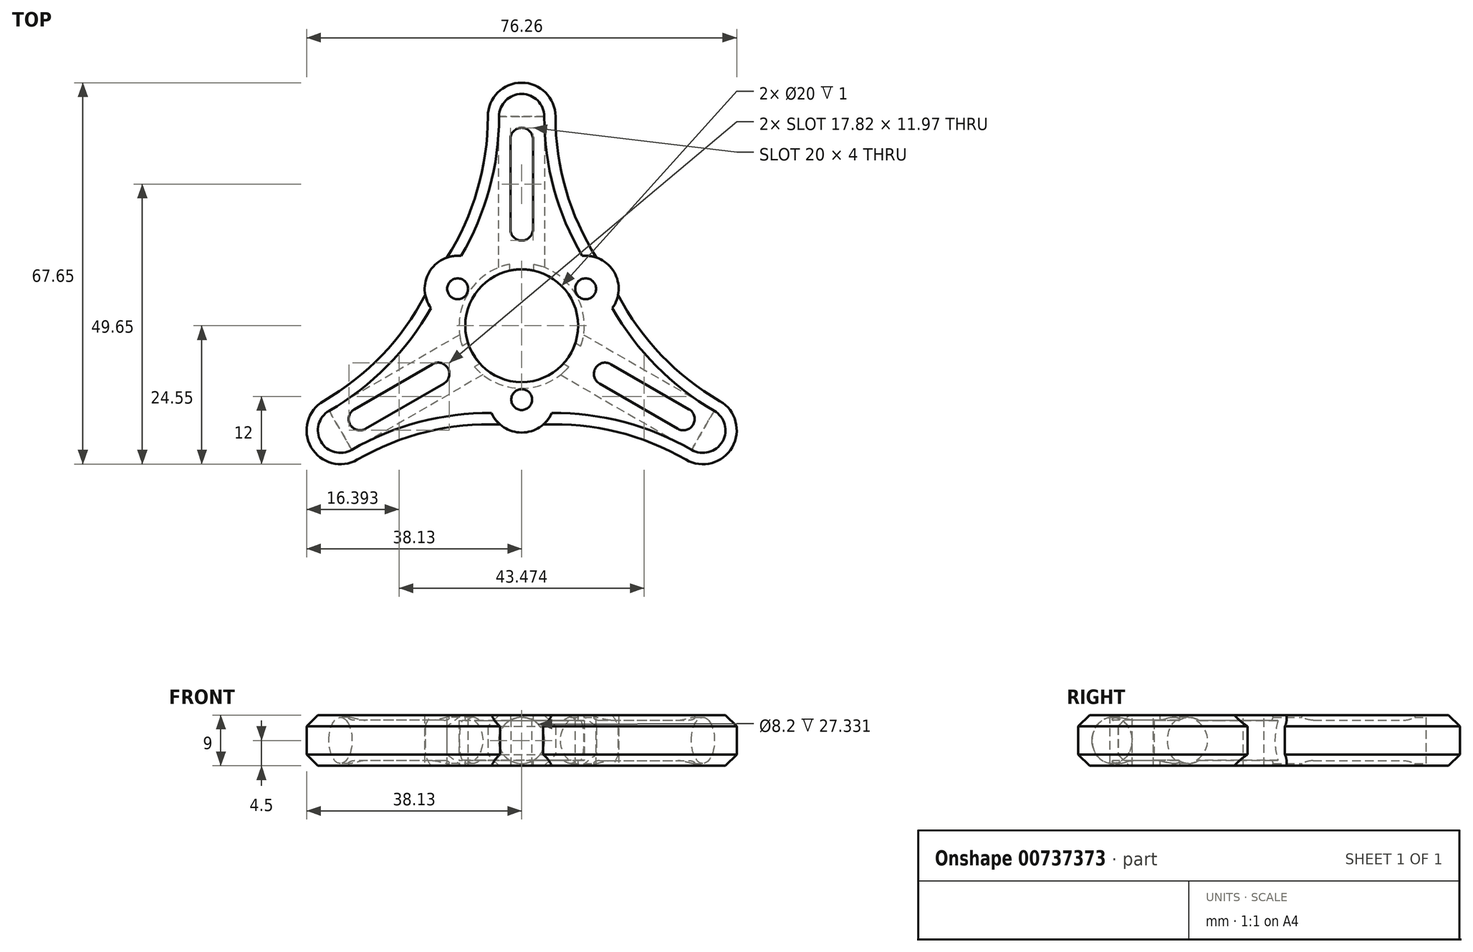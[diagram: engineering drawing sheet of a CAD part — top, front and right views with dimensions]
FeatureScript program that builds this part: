
annotation { "Feature Type Name" : "Feature", "Feature Type Description" : "" }
export const myFeature = defineFeature(function(context is Context, id is Id, definition is map)
    precondition{}
    {
        {
            var Q0;
            Q0=qCreatedBy(makeId("Top.planeOp"),FACE);
            var sketch = newSketch(context, id + "F0", { "sketchPlane" : qUnion([Q0])});
            skCircle(sketch, "E0", {"center": v(0, 0) * mm, "radius": 11.1 * mm});
            skCircle(sketch, "E1", {"center": v(0, 0) * mm, "radius": 13.1 * mm});
            skSolve(sketch);
        }
        {
            var Q0;
            Q0 = qSketchRegion(id + "F0", true);
            extrude(context, id + "F1", {"entities" : qUnion([Q0]), "depth" : 3.5 * mm, "offsetDistance" : 25 * mm});
        }
        {
            var Q0;
            Q0=makeQuery(id+"F1.opExtrude","CAP_FACE",FACE,{"disambiguationData":[OSD([sQuery(id+"F0.wireOp",EDGE,"E0"),sQuery(id+"F0.wireOp",EDGE,"E1")])],"isStart":true});
            var sketch = newSketch(context, id + "F2", { "sketchPlane" : qUnion([Q0])});
            skArc(sketch, "E2", {"start": v(8.66, 5) * mm, "mid": v(0, 10) * mm, "end": v(-8.66, 5) * mm});
            skCircle(sketch, "E3", {"center": v(0, 13.1) * mm, "radius": 1.85 * mm});
            skArc(sketch, "E4.0", {"start": v(-3.85, 12.52) * mm, "mid": v(-8.16, 10.25) * mm, "end": v(-11.34, 6.55) * mm});
            skArc(sketch, "E5", {"start": v(3.85, 13.1) * mm, "mid": v(0, 16.95) * mm, "end": v(-3.85, 13.1) * mm});
            skLineSegment(sketch, "E6", {"start": v(-3.85, 13.1) * mm, "end": v(-3.85, 12.52) * mm});
            skLineSegment(sketch, "E7", {"start": v(3.85, 13.1) * mm, "end": v(3.85, 12.52) * mm});
            skLineSegment(sketch, "E8", {"start": v(0, 0) * mm, "end": v(-31, 17.9) * mm, "construction": true});
            skLineSegment(sketch, "E9", {"start": v(0, 0) * mm, "end": v(38.49, 22.22) * mm, "construction": true});
            skArc(sketch, "E10.trimOffspring", {"start": v(11.34, 6.55) * mm, "mid": v(8.16, 10.25) * mm, "end": v(3.85, 12.52) * mm});
            skArc(sketch, "E11.1.0", {"start": v(-8.92, -9.6) * mm, "mid": v(-4.8, -12.2) * mm, "end": v(0, -13.1) * mm});
            skLineSegment(sketch, "E11.1.1", {"start": v(-9.42, -9.88) * mm, "end": v(-8.92, -9.6) * mm});
            skArc(sketch, "E11.1.2", {"start": v(-13.27, -3.22) * mm, "mid": v(-14.68, -8.47) * mm, "end": v(-9.42, -9.88) * mm});
            skLineSegment(sketch, "E11.1.3", {"start": v(-13.27, -3.22) * mm, "end": v(-12.77, -2.93) * mm});
            skArc(sketch, "E11.1.4", {"start": v(-11.34, 6.55) * mm, "mid": v(-12.95, 1.95) * mm, "end": v(-12.77, -2.93) * mm});
            skArc(sketch, "E11.1.5", {"start": v(-8.66, 5) * mm, "mid": v(-8.66, -5) * mm, "end": v(0, -10) * mm});
            skArc(sketch, "E11.2.0", {"start": v(12.77, -2.93) * mm, "mid": v(12.95, 1.95) * mm, "end": v(11.34, 6.55) * mm});
            skLineSegment(sketch, "E11.2.1", {"start": v(13.27, -3.22) * mm, "end": v(12.77, -2.93) * mm});
            skArc(sketch, "E11.2.2", {"start": v(9.42, -9.88) * mm, "mid": v(14.68, -8.47) * mm, "end": v(13.27, -3.22) * mm});
            skLineSegment(sketch, "E11.2.3", {"start": v(9.42, -9.88) * mm, "end": v(8.92, -9.6) * mm});
            skArc(sketch, "E11.2.4", {"start": v(0, -13.1) * mm, "mid": v(4.8, -12.2) * mm, "end": v(8.92, -9.6) * mm});
            skArc(sketch, "E11.2.5", {"start": v(0, -10) * mm, "mid": v(8.66, -5) * mm, "end": v(8.66, 5) * mm});
            skCircle(sketch, "E12", {"center": v(11.34, -6.55) * mm, "radius": 1.85 * mm});
            skCircle(sketch, "E13", {"center": v(-11.34, -6.55) * mm, "radius": 1.85 * mm});
            skSolve(sketch);
        }
        {
            var Q0;
            Q0 = qSketchRegion(id + "F2", true);
            extrude(context, id + "F3", {"entities" : qUnion([Q0]), "operationType" : NewBodyOperationType.ADD, "depth" : 1 * mm, "offsetDistance" : 25 * mm});
        }
        {
            var Q0;
            Q0=qCreatedBy(makeId("Top.planeOp"),FACE);
            var sketch = newSketch(context, id + "F4", { "sketchPlane" : qUnion([Q0])});
            skArc(sketch, "E14.0", {"start": v(-13.27, 3.22) * mm, "mid": v(-14.68, 8.47) * mm, "end": v(-9.42, 9.88) * mm});
            skLineSegment(sketch, "E14.1", {"start": v(-13.27, 3.22) * mm, "end": v(-12.77, 2.93) * mm});
            skLineSegment(sketch, "E14.2", {"start": v(-9.42, 9.88) * mm, "end": v(-8.92, 9.6) * mm});
            skArc(sketch, "E15.0", {"start": v(-8.92, 9.6) * mm, "mid": v(-11.34, 6.55) * mm, "end": v(-12.77, 2.93) * mm});
            skArc(sketch, "E16.1.0", {"start": v(3.85, -13.1) * mm, "mid": v(0, -16.95) * mm, "end": v(-3.85, -13.1) * mm});
            skLineSegment(sketch, "E16.1.1", {"start": v(-3.85, -13.1) * mm, "end": v(-3.85, -12.52) * mm});
            skArc(sketch, "E16.1.2", {"start": v(-3.85, -12.52) * mm, "mid": v(0, -13.1) * mm, "end": v(3.85, -12.52) * mm});
            skLineSegment(sketch, "E16.1.3", {"start": v(3.85, -13.1) * mm, "end": v(3.85, -12.52) * mm});
            skArc(sketch, "E16.2.0", {"start": v(9.42, 9.88) * mm, "mid": v(14.68, 8.47) * mm, "end": v(13.27, 3.22) * mm});
            skLineSegment(sketch, "E16.2.1", {"start": v(13.27, 3.22) * mm, "end": v(12.77, 2.93) * mm});
            skArc(sketch, "E16.2.2", {"start": v(12.77, 2.93) * mm, "mid": v(11.34, 6.55) * mm, "end": v(8.92, 9.6) * mm});
            skLineSegment(sketch, "E16.2.3", {"start": v(9.42, 9.88) * mm, "end": v(8.92, 9.6) * mm});
            skSolve(sketch);
        }
        {
            var Q0;
            Q0 = qSketchRegion(id + "F4", true);
            extrude(context, id + "F5", {"entities" : qUnion([Q0]), "operationType" : NewBodyOperationType.ADD, "depth" : 3.5 * mm, "offsetDistance" : 25 * mm});
        }
        {
            var Q0;
            Q0=makeQuery(id+"F3.opExtrude","CAP_FACE",FACE,{"disambiguationData":[OSD([sQuery(id+"F2.wireOp",EDGE,"E2"),sQuery(id+"F2.wireOp",EDGE,"E3"),sQuery(id+"F2.wireOp",EDGE,"E4.0"),sQuery(id+"F2.wireOp",EDGE,"E5"),sQuery(id+"F2.wireOp",EDGE,"E6"),sQuery(id+"F2.wireOp",EDGE,"E7"),sQuery(id+"F2.wireOp",EDGE,"E10.trimOffspring"),sQuery(id+"F2.wireOp",EDGE,"E11.1.0"),sQuery(id+"F2.wireOp",EDGE,"E11.1.1"),sQuery(id+"F2.wireOp",EDGE,"E11.1.2"),sQuery(id+"F2.wireOp",EDGE,"E11.1.3"),sQuery(id+"F2.wireOp",EDGE,"E11.1.4"),sQuery(id+"F2.wireOp",EDGE,"E11.1.5"),sQuery(id+"F2.wireOp",EDGE,"E11.2.0"),sQuery(id+"F2.wireOp",EDGE,"E11.2.1"),sQuery(id+"F2.wireOp",EDGE,"E11.2.2"),sQuery(id+"F2.wireOp",EDGE,"E11.2.3"),sQuery(id+"F2.wireOp",EDGE,"E11.2.4"),sQuery(id+"F2.wireOp",EDGE,"E11.2.5"),sQuery(id+"F2.wireOp",EDGE,"E12"),sQuery(id+"F2.wireOp",EDGE,"E13")])],"isStart":false});
            var sketch = newSketch(context, id + "F6", { "sketchPlane" : qUnion([Q0])});
            skCircle(sketch, "E17.0", {"center": v(0, 13.1) * mm, "radius": 1.85 * mm});
            skCircle(sketch, "E17.1", {"center": v(-11.34, -6.55) * mm, "radius": 1.85 * mm});
            skCircle(sketch, "E17.2", {"center": v(11.34, -6.55) * mm, "radius": 1.85 * mm});
            skSolve(sketch);
        }
        {
            var Q0;
            Q0 = qSketchRegion(id + "F6", true);
            extrude(context, id + "F7", {"entities" : qUnion([Q0]), "operationType" : NewBodyOperationType.REMOVE, "oppositeDirection" : true, "depth" : 25 * mm, "offsetDistance" : 25 * mm});
        }
        {
            var Q0;
            Q0=makeQuery(id+"F3.opExtrude","CAP_FACE",FACE,{"disambiguationData":[OSD([sQuery(id+"F2.wireOp",EDGE,"E2"),sQuery(id+"F2.wireOp",EDGE,"E3"),sQuery(id+"F2.wireOp",EDGE,"E4.0"),sQuery(id+"F2.wireOp",EDGE,"E5"),sQuery(id+"F2.wireOp",EDGE,"E6"),sQuery(id+"F2.wireOp",EDGE,"E7"),sQuery(id+"F2.wireOp",EDGE,"E10.trimOffspring"),sQuery(id+"F2.wireOp",EDGE,"E11.1.0"),sQuery(id+"F2.wireOp",EDGE,"E11.1.1"),sQuery(id+"F2.wireOp",EDGE,"E11.1.2"),sQuery(id+"F2.wireOp",EDGE,"E11.1.3"),sQuery(id+"F2.wireOp",EDGE,"E11.1.4"),sQuery(id+"F2.wireOp",EDGE,"E11.1.5"),sQuery(id+"F2.wireOp",EDGE,"E11.2.0"),sQuery(id+"F2.wireOp",EDGE,"E11.2.1"),sQuery(id+"F2.wireOp",EDGE,"E11.2.2"),sQuery(id+"F2.wireOp",EDGE,"E11.2.3"),sQuery(id+"F2.wireOp",EDGE,"E11.2.4"),sQuery(id+"F2.wireOp",EDGE,"E11.2.5"),sQuery(id+"F2.wireOp",EDGE,"E12"),sQuery(id+"F2.wireOp",EDGE,"E13")])],"isStart":false});
            var sketch = newSketch(context, id + "F8", { "sketchPlane" : qUnion([Q0])});
            skPoint(sketch, "E18.center", {"position": v(0, 0) * mm});
            skLineSegment(sketch, "E19", {"start": v(0, 0) * mm, "end": v(0, -58.79) * mm, "construction": true});
            skLineSegment(sketch, "E20.0", {"start": v(4, 0) * mm, "end": v(4, -58.79) * mm, "construction": true});
            skLineSegment(sketch, "E21.0", {"start": v(-4, 0) * mm, "end": v(-4, -58.79) * mm, "construction": true});
            skCircle(sketch, "E22", {"center": v(0, -17.1) * mm, "radius": 4 * mm, "construction": true});
            skCircle(sketch, "E23", {"center": v(0, -25.1) * mm, "radius": 4 * mm, "construction": true});
            skCircle(sketch, "E24", {"center": v(0, -33.1) * mm, "radius": 4 * mm, "construction": true});
            skLineSegment(sketch, "E25", {"start": v(-32.95, -37.1) * mm, "end": v(37.01, -37.1) * mm, "construction": true});
            skLineSegment(sketch, "E26.0", {"start": v(-6, -13.86) * mm, "end": v(-6, -37.1) * mm});
            skLineSegment(sketch, "E27.0", {"start": v(6, -13.86) * mm, "end": v(6, -37.1) * mm});
            skLineSegment(sketch, "E28", {"start": v(-6, -37.1) * mm, "end": v(6, -37.1) * mm});
            skPoint(sketch, "E29.0.end.orphan", {"position": v(-3.85, 12.52) * mm});
            skPoint(sketch, "E29.1.end.orphan", {"position": v(-3.85, 13.1) * mm});
            skPoint(sketch, "E29.2.start.orphan", {"position": v(3.85, 13.1) * mm});
            skPoint(sketch, "E29.3.end.orphan", {"position": v(12.77, -2.93) * mm});
            skPoint(sketch, "E29.3.start.orphan", {"position": v(3.85, 12.52) * mm});
            skArc(sketch, "E30.0", {"start": v(8.92, -9.6) * mm, "mid": v(0, -13.1) * mm, "end": v(-8.92, -9.6) * mm});
            skLineSegment(sketch, "E30.1", {"start": v(9.42, -9.88) * mm, "end": v(8.92, -9.6) * mm});
            skArc(sketch, "E30.2", {"start": v(9.42, -9.88) * mm, "mid": v(14.68, -8.47) * mm, "end": v(13.27, -3.22) * mm});
            skLineSegment(sketch, "E30.3", {"start": v(13.27, -3.22) * mm, "end": v(12.77, -2.93) * mm});
            skLineSegment(sketch, "E31.bottom", {"start": v(61.53, -9.1) * mm, "end": v(49.53, -9.1) * mm, "construction": true});
            skLineSegment(sketch, "E31.top", {"start": v(61.53, -18.1) * mm, "end": v(49.53, -18.1) * mm, "construction": true});
            skLineSegment(sketch, "E31.left", {"start": v(61.53, -9.1) * mm, "end": v(61.53, -18.1) * mm, "construction": true});
            skLineSegment(sketch, "E31.right", {"start": v(49.53, -9.1) * mm, "end": v(49.53, -18.1) * mm, "construction": true});
            skPoint(sketch, "E31.middle", {"position": v(55.53, -13.6) * mm});
            skCircle(sketch, "E32", {"center": v(55.53, -13.6) * mm, "radius": 4 * mm, "construction": true});
            skLineSegment(sketch, "E33", {"start": v(0, 0) * mm, "end": v(-30.21, -32.5) * mm, "construction": true});
            skLineSegment(sketch, "E34", {"start": v(0, 0) * mm, "end": v(43.16, -9.9) * mm, "construction": true});
            skArc(sketch, "E35", {"start": v(-9.18, -11.99) * mm, "mid": v(-7.65, -13.02) * mm, "end": v(-6, -13.86) * mm});
            skArc(sketch, "E36.trimOffspring", {"start": v(14.57, -3.97) * mm, "mid": v(14.65, -3.67) * mm, "end": v(14.72, -3.37) * mm});
            skArc(sketch, "E37", {"start": v(9.18, -11.99) * mm, "mid": v(15.71, -10.44) * mm, "end": v(16.5, -3.78) * mm});
            skArc(sketch, "E38.trimOffspring", {"start": v(6, -13.86) * mm, "mid": v(7.65, -13.02) * mm, "end": v(9.18, -11.99) * mm});
            skArc(sketch, "E39", {"start": v(-11.52, -12.4) * mm, "mid": v(-10.33, -12.31) * mm, "end": v(-9.18, -11.99) * mm});
            skArc(sketch, "E40.1.0", {"start": v(16.5, -3.78) * mm, "mid": v(15.83, -2.8) * mm, "end": v(14.97, -1.96) * mm});
            skArc(sketch, "E40.1.1", {"start": v(14.97, -1.96) * mm, "mid": v(15.1, -0.11) * mm, "end": v(15, 1.73) * mm});
            skLineSegment(sketch, "E40.1.2", {"start": v(15, 1.73) * mm, "end": v(35.13, 13.35) * mm});
            skLineSegment(sketch, "E40.1.3", {"start": v(9, 12.12) * mm, "end": v(29.13, 23.75) * mm});
            skArc(sketch, "E40.1.4", {"start": v(9, 12.12) * mm, "mid": v(7.45, 13.13) * mm, "end": v(5.79, 13.95) * mm});
            skArc(sketch, "E40.1.5", {"start": v(5.79, 13.95) * mm, "mid": v(1.19, 18.83) * mm, "end": v(-4.97, 16.18) * mm});
            skLineSegment(sketch, "E40.1.6", {"start": v(-3.85, 13.1) * mm, "end": v(-3.85, 12.52) * mm});
            skArc(sketch, "E40.1.7", {"start": v(3.85, 13.1) * mm, "mid": v(0, 16.95) * mm, "end": v(-3.85, 13.1) * mm});
            skLineSegment(sketch, "E40.1.8", {"start": v(3.85, 13.1) * mm, "end": v(3.85, 12.52) * mm});
            skArc(sketch, "E40.1.9", {"start": v(3.85, 12.52) * mm, "mid": v(11.34, 6.55) * mm, "end": v(12.77, -2.93) * mm});
            skArc(sketch, "E40.2.0", {"start": v(-4.97, 16.18) * mm, "mid": v(-5.5, 15.1) * mm, "end": v(-5.79, 13.95) * mm});
            skArc(sketch, "E40.2.1", {"start": v(-5.79, 13.95) * mm, "mid": v(-7.45, 13.13) * mm, "end": v(-9, 12.12) * mm});
            skLineSegment(sketch, "E40.2.2", {"start": v(-9, 12.12) * mm, "end": v(-29.13, 23.75) * mm});
            skLineSegment(sketch, "E40.2.3", {"start": v(-15, 1.73) * mm, "end": v(-35.13, 13.35) * mm});
            skArc(sketch, "E40.2.4", {"start": v(-15, 1.73) * mm, "mid": v(-15.1, -0.11) * mm, "end": v(-14.97, -1.96) * mm});
            skArc(sketch, "E40.2.5", {"start": v(-14.97, -1.96) * mm, "mid": v(-16.9, -8.39) * mm, "end": v(-11.52, -12.4) * mm});
            skLineSegment(sketch, "E40.2.6", {"start": v(-9.42, -9.88) * mm, "end": v(-8.92, -9.6) * mm});
            skArc(sketch, "E40.2.7", {"start": v(-13.27, -3.22) * mm, "mid": v(-14.68, -8.48) * mm, "end": v(-9.42, -9.88) * mm});
            skLineSegment(sketch, "E40.2.8", {"start": v(-13.27, -3.22) * mm, "end": v(-12.77, -2.93) * mm});
            skArc(sketch, "E40.2.9", {"start": v(-12.77, -2.93) * mm, "mid": v(-11.34, 6.55) * mm, "end": v(-3.85, 12.52) * mm});
            skLineSegment(sketch, "E41", {"start": v(-35.13, 13.35) * mm, "end": v(-29.13, 23.75) * mm});
            skLineSegment(sketch, "E42", {"start": v(29.13, 23.75) * mm, "end": v(35.13, 13.35) * mm});
            skSolve(sketch);
        }
        {
            var Q0;
            Q0 = qSketchRegion(id + "F8", true);
            extrude(context, id + "F9", {"entities" : qUnion([Q0]), "oppositeDirection" : true, "depth" : 9 * mm, "offsetDistance" : 25 * mm});
        }
        {
            var Q0;
            Q0=makeQuery(id+"F9.opExtrude","CAP_FACE",FACE,{"disambiguationData":[OSD([sQuery(id+"F8.wireOp",EDGE,"E26.0"),sQuery(id+"F8.wireOp",EDGE,"E27.0"),sQuery(id+"F8.wireOp",EDGE,"E28"),sQuery(id+"F8.wireOp",EDGE,"E30.0"),sQuery(id+"F8.wireOp",EDGE,"E30.1"),sQuery(id+"F8.wireOp",EDGE,"E30.2"),sQuery(id+"F8.wireOp",EDGE,"E30.3"),sQuery(id+"F8.wireOp",EDGE,"E35"),sQuery(id+"F8.wireOp",EDGE,"E37"),sQuery(id+"F8.wireOp",EDGE,"E38.trimOffspring"),sQuery(id+"F8.wireOp",EDGE,"E39"),sQuery(id+"F8.wireOp",EDGE,"E40.1.0"),sQuery(id+"F8.wireOp",EDGE,"E40.1.1"),sQuery(id+"F8.wireOp",EDGE,"E40.1.2"),sQuery(id+"F8.wireOp",EDGE,"E40.1.3"),sQuery(id+"F8.wireOp",EDGE,"E40.1.4"),sQuery(id+"F8.wireOp",EDGE,"E40.1.5"),sQuery(id+"F8.wireOp",EDGE,"E40.1.6"),sQuery(id+"F8.wireOp",EDGE,"E40.1.7"),sQuery(id+"F8.wireOp",EDGE,"E40.1.8"),sQuery(id+"F8.wireOp",EDGE,"E40.1.9"),sQuery(id+"F8.wireOp",EDGE,"E40.2.0"),sQuery(id+"F8.wireOp",EDGE,"E40.2.1"),sQuery(id+"F8.wireOp",EDGE,"E40.2.2"),sQuery(id+"F8.wireOp",EDGE,"E40.2.3"),sQuery(id+"F8.wireOp",EDGE,"E40.2.4"),sQuery(id+"F8.wireOp",EDGE,"E40.2.5"),sQuery(id+"F8.wireOp",EDGE,"E40.2.6"),sQuery(id+"F8.wireOp",EDGE,"E40.2.7"),sQuery(id+"F8.wireOp",EDGE,"E40.2.8"),sQuery(id+"F8.wireOp",EDGE,"E40.2.9"),sQuery(id+"F8.wireOp",EDGE,"E41"),sQuery(id+"F8.wireOp",EDGE,"E42")])],"isStart":false});
            var sketch = newSketch(context, id + "F10", { "sketchPlane" : qUnion([Q0])});
            skArc(sketch, "E43.0", {"start": v(8.92, 9.6) * mm, "mid": v(0, 13.1) * mm, "end": v(-8.92, 9.6) * mm});
            skLineSegment(sketch, "E43.1", {"start": v(9.42, 9.88) * mm, "end": v(8.92, 9.6) * mm});
            skArc(sketch, "E43.2", {"start": v(9.42, 9.88) * mm, "mid": v(14.68, 8.47) * mm, "end": v(13.27, 3.22) * mm});
            skLineSegment(sketch, "E43.3", {"start": v(13.27, 3.22) * mm, "end": v(12.77, 2.93) * mm});
            skCircle(sketch, "E43.4", {"center": v(11.34, 6.55) * mm, "radius": 1.85 * mm});
            skCircle(sketch, "E44.0", {"center": v(0, 0) * mm, "radius": 11.1 * mm});
            skArc(sketch, "E45.1.0", {"start": v(-12.77, 2.93) * mm, "mid": v(-11.34, -6.55) * mm, "end": v(-3.85, -12.52) * mm});
            skLineSegment(sketch, "E45.1.1", {"start": v(-13.27, 3.22) * mm, "end": v(-12.77, 2.93) * mm});
            skArc(sketch, "E45.1.2", {"start": v(-13.27, 3.22) * mm, "mid": v(-14.68, 8.48) * mm, "end": v(-9.42, 9.88) * mm});
            skLineSegment(sketch, "E45.1.3", {"start": v(-9.42, 9.88) * mm, "end": v(-8.92, 9.6) * mm});
            skArc(sketch, "E45.2.0", {"start": v(3.85, -12.52) * mm, "mid": v(11.34, -6.55) * mm, "end": v(12.77, 2.93) * mm});
            skLineSegment(sketch, "E45.2.1", {"start": v(3.85, -13.1) * mm, "end": v(3.85, -12.52) * mm});
            skArc(sketch, "E45.2.2", {"start": v(3.85, -13.1) * mm, "mid": v(0, -16.95) * mm, "end": v(-3.85, -13.1) * mm});
            skLineSegment(sketch, "E45.2.3", {"start": v(-3.85, -13.1) * mm, "end": v(-3.85, -12.52) * mm});
            skCircle(sketch, "E46.0", {"center": v(-11.34, 6.55) * mm, "radius": 1.85 * mm});
            skCircle(sketch, "E46.1", {"center": v(0, -13.1) * mm, "radius": 1.85 * mm});
            skSolve(sketch);
        }
        {
            var Q0;
            Q0 = qSketchRegion(id + "F10", true);
            extrude(context, id + "F11", {"entities" : qUnion([Q0]), "operationType" : NewBodyOperationType.ADD, "oppositeDirection" : true, "depth" : 4.5 * mm, "offsetDistance" : 25 * mm});
        }
        {
            var Q0;
            Q0=makeQuery(id+"F11.boolean.opBoolean","MERGE",FACE,{"derivedFrom":[makeQuery(id+"F9.opExtrude","CAP_FACE",FACE,{"disambiguationData":[OSD([sQuery(id+"F8.wireOp",EDGE,"E26.0"),sQuery(id+"F8.wireOp",EDGE,"E27.0"),sQuery(id+"F8.wireOp",EDGE,"E28"),sQuery(id+"F8.wireOp",EDGE,"E30.0"),sQuery(id+"F8.wireOp",EDGE,"E30.1"),sQuery(id+"F8.wireOp",EDGE,"E30.2"),sQuery(id+"F8.wireOp",EDGE,"E30.3"),sQuery(id+"F8.wireOp",EDGE,"E35"),sQuery(id+"F8.wireOp",EDGE,"E37"),sQuery(id+"F8.wireOp",EDGE,"E38.trimOffspring"),sQuery(id+"F8.wireOp",EDGE,"E39"),sQuery(id+"F8.wireOp",EDGE,"E40.1.0"),sQuery(id+"F8.wireOp",EDGE,"E40.1.1"),sQuery(id+"F8.wireOp",EDGE,"E40.1.2"),sQuery(id+"F8.wireOp",EDGE,"E40.1.3"),sQuery(id+"F8.wireOp",EDGE,"E40.1.4"),sQuery(id+"F8.wireOp",EDGE,"E40.1.5"),sQuery(id+"F8.wireOp",EDGE,"E40.1.6"),sQuery(id+"F8.wireOp",EDGE,"E40.1.7"),sQuery(id+"F8.wireOp",EDGE,"E40.1.8"),sQuery(id+"F8.wireOp",EDGE,"E40.1.9"),sQuery(id+"F8.wireOp",EDGE,"E40.2.0"),sQuery(id+"F8.wireOp",EDGE,"E40.2.1"),sQuery(id+"F8.wireOp",EDGE,"E40.2.2"),sQuery(id+"F8.wireOp",EDGE,"E40.2.3"),sQuery(id+"F8.wireOp",EDGE,"E40.2.4"),sQuery(id+"F8.wireOp",EDGE,"E40.2.5"),sQuery(id+"F8.wireOp",EDGE,"E40.2.6"),sQuery(id+"F8.wireOp",EDGE,"E40.2.7"),sQuery(id+"F8.wireOp",EDGE,"E40.2.8"),sQuery(id+"F8.wireOp",EDGE,"E40.2.9"),sQuery(id+"F8.wireOp",EDGE,"E41"),sQuery(id+"F8.wireOp",EDGE,"E42")])],"isStart":false}),makeQuery(id+"F11.opExtrude","CAP_FACE",FACE,{"disambiguationData":[OSD([sQuery(id+"F10.wireOp",EDGE,"E43.0"),sQuery(id+"F10.wireOp",EDGE,"E43.1"),sQuery(id+"F10.wireOp",EDGE,"E43.2"),sQuery(id+"F10.wireOp",EDGE,"E43.3"),sQuery(id+"F10.wireOp",EDGE,"E43.4"),sQuery(id+"F10.wireOp",EDGE,"E44.0"),sQuery(id+"F10.wireOp",EDGE,"E45.1.0"),sQuery(id+"F10.wireOp",EDGE,"E45.1.1"),sQuery(id+"F10.wireOp",EDGE,"E45.1.2"),sQuery(id+"F10.wireOp",EDGE,"E45.1.3"),sQuery(id+"F10.wireOp",EDGE,"E45.2.0"),sQuery(id+"F10.wireOp",EDGE,"E45.2.1"),sQuery(id+"F10.wireOp",EDGE,"E45.2.2"),sQuery(id+"F10.wireOp",EDGE,"E45.2.3"),sQuery(id+"F10.wireOp",EDGE,"E46.0"),sQuery(id+"F10.wireOp",EDGE,"E46.1")])],"isStart":true})]});
            var sketch = newSketch(context, id + "F12", { "sketchPlane" : qUnion([Q0])});
            skCircle(sketch, "E47", {"center": v(0, 0) * mm, "radius": 10 * mm});
            skCircle(sketch, "E48.0", {"center": v(0, 0) * mm, "radius": 11.1 * mm});
            skSolve(sketch);
        }
        {
            var Q0;
            Q0 = qSketchRegion(id + "F12", true);
            extrude(context, id + "F13", {"entities" : qUnion([Q0]), "operationType" : NewBodyOperationType.ADD, "oppositeDirection" : true, "depth" : 1 * mm, "offsetDistance" : 25 * mm});
        }
        {
            var Q0;
            Q0=makeQuery(id+"F9.opExtrude","SWEPT_FACE",FACE,{"disambiguationData":[OSD([sQuery(id+"F8.wireOp",EDGE,"E28")])]});
            var sketch = newSketch(context, id + "F14", { "sketchPlane" : qUnion([Q0])});
            skLineSegment(sketch, "E49", {"start": v(0, -1) * mm, "end": v(0, 8) * mm, "construction": true});
            skCircle(sketch, "E50", {"center": v(0, 3.5) * mm, "radius": 4.1 * mm});
            skSolve(sketch);
        }
        {
            var Q0;
            Q0 = qSketchRegion(id + "F14", true);
            extrude(context, id + "F15", {"entities" : qUnion([Q0]), "oppositeDirection" : true, "depth" : 36.8 * mm, "offsetDistance" : 25 * mm});
        }
        {
            var Q0;
            Q0=makeQuery(id+"F9.opExtrude","CAP_FACE",FACE,{"disambiguationData":[OSD([sQuery(id+"F8.wireOp",EDGE,"E26.0"),sQuery(id+"F8.wireOp",EDGE,"E27.0"),sQuery(id+"F8.wireOp",EDGE,"E28"),sQuery(id+"F8.wireOp",EDGE,"E30.0"),sQuery(id+"F8.wireOp",EDGE,"E30.1"),sQuery(id+"F8.wireOp",EDGE,"E30.2"),sQuery(id+"F8.wireOp",EDGE,"E30.3"),sQuery(id+"F8.wireOp",EDGE,"E35"),sQuery(id+"F8.wireOp",EDGE,"E37"),sQuery(id+"F8.wireOp",EDGE,"E38.trimOffspring"),sQuery(id+"F8.wireOp",EDGE,"E39"),sQuery(id+"F8.wireOp",EDGE,"E40.1.0"),sQuery(id+"F8.wireOp",EDGE,"E40.1.1"),sQuery(id+"F8.wireOp",EDGE,"E40.1.2"),sQuery(id+"F8.wireOp",EDGE,"E40.1.3"),sQuery(id+"F8.wireOp",EDGE,"E40.1.4"),sQuery(id+"F8.wireOp",EDGE,"E40.1.5"),sQuery(id+"F8.wireOp",EDGE,"E40.1.6"),sQuery(id+"F8.wireOp",EDGE,"E40.1.7"),sQuery(id+"F8.wireOp",EDGE,"E40.1.8"),sQuery(id+"F8.wireOp",EDGE,"E40.1.9"),sQuery(id+"F8.wireOp",EDGE,"E40.2.0"),sQuery(id+"F8.wireOp",EDGE,"E40.2.1"),sQuery(id+"F8.wireOp",EDGE,"E40.2.2"),sQuery(id+"F8.wireOp",EDGE,"E40.2.3"),sQuery(id+"F8.wireOp",EDGE,"E40.2.4"),sQuery(id+"F8.wireOp",EDGE,"E40.2.5"),sQuery(id+"F8.wireOp",EDGE,"E40.2.6"),sQuery(id+"F8.wireOp",EDGE,"E40.2.7"),sQuery(id+"F8.wireOp",EDGE,"E40.2.8"),sQuery(id+"F8.wireOp",EDGE,"E40.2.9"),sQuery(id+"F8.wireOp",EDGE,"E41"),sQuery(id+"F8.wireOp",EDGE,"E42")])],"isStart":true});
            var sketch = newSketch(context, id + "F16", { "sketchPlane" : qUnion([Q0])});
            skLineSegment(sketch, "E51.bottom", {"start": v(-2, -15.1) * mm, "end": v(2, -15.1) * mm});
            skLineSegment(sketch, "E51.top", {"start": v(-2, -35.1) * mm, "end": v(2, -35.1) * mm});
            skLineSegment(sketch, "E51.left", {"start": v(-2, -15.1) * mm, "end": v(-2, -35.1) * mm});
            skLineSegment(sketch, "E51.right", {"start": v(2, -15.1) * mm, "end": v(2, -35.1) * mm});
            skPoint(sketch, "E51.middle", {"position": v(0, -25.1) * mm});
            skLineSegment(sketch, "E52", {"start": v(0, -37.1) * mm, "end": v(0, -13.1) * mm, "construction": true});
            skSolve(sketch);
        }
        {
            var Q0;
            Q0=qCreatedBy(makeId("Front.planeOp"),FACE);
            var sketch = newSketch(context, id + "F17", { "sketchPlane" : qUnion([Q0])});
            skLineSegment(sketch, "E53", {"start": v(0, 0) * mm, "end": v(0, 48.44) * mm});
            skSolve(sketch);
        }
        {
            var Q0;
            Q0 = qSketchRegion(id + "F16", true);
            extrude(context, id + "F18", {"entities" : qUnion([Q0]), "endBound" : BoundingType.SYMMETRIC, "oppositeDirection" : true, "depth" : 25 * mm, "offsetDistance" : 25 * mm});
        }
        {
            var Q0;
            Q0=makeQuery(id+"F18.opExtrude","SWEPT_EDGE",EDGE,{"disambiguationData":[OSD([sQuery(id+"F16.wireOp",EDGE,"E51.top"),sQuery(id+"F16.wireOp",EDGE,"E51.left")])]});
            var Q1;
            Q1=makeQuery(id+"F18.opExtrude","SWEPT_EDGE",EDGE,{"disambiguationData":[OSD([sQuery(id+"F16.wireOp",EDGE,"E51.top"),sQuery(id+"F16.wireOp",EDGE,"E51.right")])]});
            var Q2;
            Q2=makeQuery(id+"F18.opExtrude","SWEPT_EDGE",EDGE,{"disambiguationData":[OSD([sQuery(id+"F16.wireOp",EDGE,"E51.bottom"),sQuery(id+"F16.wireOp",EDGE,"E51.left")])]});
            var Q3;
            Q3=makeQuery(id+"F18.opExtrude","SWEPT_EDGE",EDGE,{"disambiguationData":[OSD([sQuery(id+"F16.wireOp",EDGE,"E51.bottom"),sQuery(id+"F16.wireOp",EDGE,"E51.right")])]});
            fillet(context, id + "F19", {"entities" : qUnion([Q0, Q1, Q2, Q3]), "radius" : 2 * mm, "tangentPropagation" : true, "allowEdgeOverflow" : false});
        }
        {
            var Q0;
            Q0=makeQuery(id+"F15.opExtrude","SWEPT_BODY",BODY,{"disambiguationData":[OSD([sQuery(id+"F14.wireOp",EDGE,"E50")])]});
            var Q1;
            Q1=makeQuery(id+"F18.opExtrude","SWEPT_BODY",BODY,{"disambiguationData":[OSD([sQuery(id+"F16.wireOp",EDGE,"E51.bottom"),sQuery(id+"F16.wireOp",EDGE,"E51.top"),sQuery(id+"F16.wireOp",EDGE,"E51.left"),sQuery(id+"F16.wireOp",EDGE,"E51.right")])]});
            var Q2;
            Q2=sQuery(id+"F17.wireOp",EDGE,"E53");
            circularPattern(context, id + "F20", {"operationType" : NewBodyOperationType.REMOVE, "entities" : qUnion([Q0, Q1]), "axis" : qUnion([Q2]), "angle" : 360 * degree, "instanceCount" : 3, "equalSpace" : true});
        }
        {
            var Q0;
            Q0=makeQuery(id+"F9.opExtrude","CAP_FACE",FACE,{"disambiguationData":[OSD([sQuery(id+"F8.wireOp",EDGE,"E26.0"),sQuery(id+"F8.wireOp",EDGE,"E27.0"),sQuery(id+"F8.wireOp",EDGE,"E28"),sQuery(id+"F8.wireOp",EDGE,"E30.0"),sQuery(id+"F8.wireOp",EDGE,"E30.1"),sQuery(id+"F8.wireOp",EDGE,"E30.2"),sQuery(id+"F8.wireOp",EDGE,"E30.3"),sQuery(id+"F8.wireOp",EDGE,"E35"),sQuery(id+"F8.wireOp",EDGE,"E37"),sQuery(id+"F8.wireOp",EDGE,"E38.trimOffspring"),sQuery(id+"F8.wireOp",EDGE,"E39"),sQuery(id+"F8.wireOp",EDGE,"E40.1.0"),sQuery(id+"F8.wireOp",EDGE,"E40.1.1"),sQuery(id+"F8.wireOp",EDGE,"E40.1.2"),sQuery(id+"F8.wireOp",EDGE,"E40.1.3"),sQuery(id+"F8.wireOp",EDGE,"E40.1.4"),sQuery(id+"F8.wireOp",EDGE,"E40.1.5"),sQuery(id+"F8.wireOp",EDGE,"E40.1.6"),sQuery(id+"F8.wireOp",EDGE,"E40.1.7"),sQuery(id+"F8.wireOp",EDGE,"E40.1.8"),sQuery(id+"F8.wireOp",EDGE,"E40.1.9"),sQuery(id+"F8.wireOp",EDGE,"E40.2.0"),sQuery(id+"F8.wireOp",EDGE,"E40.2.1"),sQuery(id+"F8.wireOp",EDGE,"E40.2.2"),sQuery(id+"F8.wireOp",EDGE,"E40.2.3"),sQuery(id+"F8.wireOp",EDGE,"E40.2.4"),sQuery(id+"F8.wireOp",EDGE,"E40.2.5"),sQuery(id+"F8.wireOp",EDGE,"E40.2.6"),sQuery(id+"F8.wireOp",EDGE,"E40.2.7"),sQuery(id+"F8.wireOp",EDGE,"E40.2.8"),sQuery(id+"F8.wireOp",EDGE,"E40.2.9"),sQuery(id+"F8.wireOp",EDGE,"E41"),sQuery(id+"F8.wireOp",EDGE,"E42")])],"isStart":true});
            var sketch = newSketch(context, id + "F21", { "sketchPlane" : qUnion([Q0])});
            skLineSegment(sketch, "E54.0", {"start": v(-6, -37.1) * mm, "end": v(6, -37.1) * mm});
            skArc(sketch, "E55", {"start": v(-6, -37.1) * mm, "mid": v(0, -43.1) * mm, "end": v(6, -37.1) * mm});
            skArc(sketch, "E56.1.0", {"start": v(35.13, 13.35) * mm, "mid": v(37.33, 21.55) * mm, "end": v(29.13, 23.75) * mm});
            skLineSegment(sketch, "E56.1.1", {"start": v(35.13, 13.35) * mm, "end": v(29.13, 23.75) * mm});
            skArc(sketch, "E56.2.0", {"start": v(-29.13, 23.75) * mm, "mid": v(-37.33, 21.55) * mm, "end": v(-35.13, 13.35) * mm});
            skLineSegment(sketch, "E56.2.1", {"start": v(-29.13, 23.75) * mm, "end": v(-35.13, 13.35) * mm});
            skPoint(sketch, "E56.center", {"position": v(0, 0) * mm});
            skSolve(sketch);
        }
        {
            var Q0;
            Q0 = qSketchRegion(id + "F21", true);
            extrude(context, id + "F22", {"entities" : qUnion([Q0]), "operationType" : NewBodyOperationType.ADD, "oppositeDirection" : true, "depth" : 9 * mm, "offsetDistance" : 25 * mm});
        }
        {
            var Q0;
            Q0=makeQuery(id+"F22.boolean.opBoolean","MERGE",FACE,{"derivedFrom":[makeQuery(id+"F9.opExtrude","CAP_FACE",FACE,{"disambiguationData":[OSD([sQuery(id+"F8.wireOp",EDGE,"E26.0"),sQuery(id+"F8.wireOp",EDGE,"E27.0"),sQuery(id+"F8.wireOp",EDGE,"E28"),sQuery(id+"F8.wireOp",EDGE,"E30.0"),sQuery(id+"F8.wireOp",EDGE,"E30.1"),sQuery(id+"F8.wireOp",EDGE,"E30.2"),sQuery(id+"F8.wireOp",EDGE,"E30.3"),sQuery(id+"F8.wireOp",EDGE,"E35"),sQuery(id+"F8.wireOp",EDGE,"E37"),sQuery(id+"F8.wireOp",EDGE,"E38.trimOffspring"),sQuery(id+"F8.wireOp",EDGE,"E39"),sQuery(id+"F8.wireOp",EDGE,"E40.1.0"),sQuery(id+"F8.wireOp",EDGE,"E40.1.1"),sQuery(id+"F8.wireOp",EDGE,"E40.1.2"),sQuery(id+"F8.wireOp",EDGE,"E40.1.3"),sQuery(id+"F8.wireOp",EDGE,"E40.1.4"),sQuery(id+"F8.wireOp",EDGE,"E40.1.5"),sQuery(id+"F8.wireOp",EDGE,"E40.1.6"),sQuery(id+"F8.wireOp",EDGE,"E40.1.7"),sQuery(id+"F8.wireOp",EDGE,"E40.1.8"),sQuery(id+"F8.wireOp",EDGE,"E40.1.9"),sQuery(id+"F8.wireOp",EDGE,"E40.2.0"),sQuery(id+"F8.wireOp",EDGE,"E40.2.1"),sQuery(id+"F8.wireOp",EDGE,"E40.2.2"),sQuery(id+"F8.wireOp",EDGE,"E40.2.3"),sQuery(id+"F8.wireOp",EDGE,"E40.2.4"),sQuery(id+"F8.wireOp",EDGE,"E40.2.5"),sQuery(id+"F8.wireOp",EDGE,"E40.2.6"),sQuery(id+"F8.wireOp",EDGE,"E40.2.7"),sQuery(id+"F8.wireOp",EDGE,"E40.2.8"),sQuery(id+"F8.wireOp",EDGE,"E40.2.9"),sQuery(id+"F8.wireOp",EDGE,"E41"),sQuery(id+"F8.wireOp",EDGE,"E42")])],"isStart":true}),makeQuery(id+"F22.opExtrude","CAP_FACE",FACE,{"disambiguationData":[OSD([sQuery(id+"F21.wireOp",EDGE,"E54.0"),sQuery(id+"F21.wireOp",EDGE,"E55")])],"isStart":true}),makeQuery(id+"F22.opExtrude","CAP_FACE",FACE,{"disambiguationData":[OSD([sQuery(id+"F21.wireOp",EDGE,"E56.1.0"),sQuery(id+"F21.wireOp",EDGE,"E56.1.1")])],"isStart":true}),makeQuery(id+"F22.opExtrude","CAP_FACE",FACE,{"disambiguationData":[OSD([sQuery(id+"F21.wireOp",EDGE,"E56.2.0"),sQuery(id+"F21.wireOp",EDGE,"E56.2.1")])],"isStart":true})]});
            var sketch = newSketch(context, id + "F23", { "sketchPlane" : qUnion([Q0])});
            skPoint(sketch, "E57.endSnap0", {"position": v(16.41, -9.48) * mm});
            skArc(sketch, "E58.0", {"start": v(9.18, -11.99) * mm, "mid": v(13.26, -12.08) * mm, "end": v(16.41, -9.48) * mm});
            skArc(sketch, "E58.1", {"start": v(6, -13.86) * mm, "mid": v(7.65, -13.02) * mm, "end": v(9.18, -11.99) * mm});
            skLineSegment(sketch, "E58.2", {"start": v(6, -13.86) * mm, "end": v(6, -37.1) * mm});
            skArc(sketch, "E58.3", {"start": v(-6, -37.1) * mm, "mid": v(0, -43.1) * mm, "end": v(6, -37.1) * mm});
            skLineSegment(sketch, "E58.4", {"start": v(-6, -13.86) * mm, "end": v(-6, -37.1) * mm});
            skArc(sketch, "E58.5", {"start": v(-9.18, -11.99) * mm, "mid": v(-7.65, -13.02) * mm, "end": v(-6, -13.86) * mm});
            skArc(sketch, "E58.6", {"start": v(-16.41, -9.48) * mm, "mid": v(-13.26, -12.08) * mm, "end": v(-9.18, -11.99) * mm});
            skPoint(sketch, "E59", {"position": v(-16.41, -9.47) * mm});
            skPoint(sketch, "E60.orphan", {"position": v(14.97, -1.96) * mm});
            skPoint(sketch, "E61.orphan", {"position": v(-14.97, -1.96) * mm});
            skLineSegment(sketch, "E62", {"start": v(0, 0) * mm, "end": v(0, -47.52) * mm, "construction": true});
            skPoint(sketch, "E62.endSnap0", {"position": v(0, -43.1) * mm});
            skArc(sketch, "E63", {"start": v(-6, -37.1) * mm, "mid": v(-7.85, -24.07) * mm, "end": v(-13.26, -12.08) * mm});
            skArc(sketch, "E64.MirrorCS", {"start": v(6, -37.1) * mm, "mid": v(7.85, -24.07) * mm, "end": v(13.26, -12.08) * mm});
            skSolve(sketch);
        }
        {
            var Q0;
            Q0 = qSketchRegion(id + "F23", true);
            extrude(context, id + "F24", {"entities" : qUnion([Q0]), "oppositeDirection" : true, "depth" : 9 * mm, "offsetDistance" : 25 * mm});
        }
        {
            var Q0;
            Q0=makeQuery(id+"F24.opExtrude","SWEPT_BODY",BODY,{"disambiguationData":[OSD([sQuery(id+"F23.wireOp",EDGE,"E58.0"),sQuery(id+"F23.wireOp",EDGE,"E58.1"),sQuery(id+"F23.wireOp",EDGE,"E58.2"),sQuery(id+"F23.wireOp",EDGE,"E64.MirrorCS")])]});
            var Q1;
            Q1=makeQuery(id+"F24.opExtrude","SWEPT_BODY",BODY,{"disambiguationData":[OSD([sQuery(id+"F23.wireOp",EDGE,"E58.4"),sQuery(id+"F23.wireOp",EDGE,"E58.5"),sQuery(id+"F23.wireOp",EDGE,"E58.6"),sQuery(id+"F23.wireOp",EDGE,"E63")])]});
            var Q2;
            Q2=sQuery(id+"F17.wireOp",EDGE,"E53");
            circularPattern(context, id + "F25", {"operationType" : NewBodyOperationType.ADD, "entities" : qUnion([Q0, Q1]), "axis" : qUnion([Q2]), "angle" : 360 * degree, "instanceCount" : 3, "equalSpace" : true});
        }
        {
            var Q0;
            Q0=makeQuery(id+"F25.opPattern","COPY",EDGE,{"derivedFrom":makeQuery(id+"F24.opExtrude","CAP_EDGE",EDGE,{"disambiguationData":[OSD([sQuery(id+"F23.wireOp",EDGE,"E64.MirrorCS")])],"isStart":false}),"instanceName":"2"});
            var Q1;
            Q1=makeQuery(id+"F24.opExtrude","CAP_EDGE",EDGE,{"disambiguationData":[OSD([sQuery(id+"F23.wireOp",EDGE,"E64.MirrorCS")])],"isStart":false});
            var Q2;
            Q2=makeQuery(id+"F25.opPattern","COPY",EDGE,{"derivedFrom":makeQuery(id+"F24.opExtrude","CAP_EDGE",EDGE,{"disambiguationData":[OSD([sQuery(id+"F23.wireOp",EDGE,"E64.MirrorCS")])],"isStart":false}),"instanceName":"1"});
            var Q3;
            Q3=makeQuery(id+"F24.opExtrude","CAP_EDGE",EDGE,{"disambiguationData":[OSD([sQuery(id+"F23.wireOp",EDGE,"E63")])],"isStart":true});
            var Q4;
            Q4=makeQuery(id+"F25.opPattern","COPY",EDGE,{"derivedFrom":makeQuery(id+"F24.opExtrude","CAP_EDGE",EDGE,{"disambiguationData":[OSD([sQuery(id+"F23.wireOp",EDGE,"E64.MirrorCS")])],"isStart":true}),"instanceName":"1"});
            var Q5;
            Q5=makeQuery(id+"F25.opPattern","COPY",EDGE,{"derivedFrom":makeQuery(id+"F24.opExtrude","CAP_EDGE",EDGE,{"disambiguationData":[OSD([sQuery(id+"F23.wireOp",EDGE,"E64.MirrorCS")])],"isStart":true}),"instanceName":"2"});
            chamfer(context, id + "F26", {"entities" : qUnion([Q0, Q1, Q2, Q3, Q4, Q5]), "width" : 2 * mm, "tangentPropagation" : true});
        }
    });
